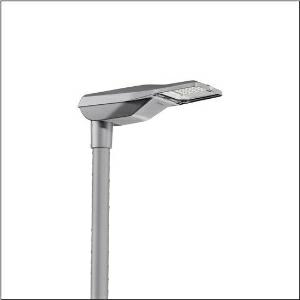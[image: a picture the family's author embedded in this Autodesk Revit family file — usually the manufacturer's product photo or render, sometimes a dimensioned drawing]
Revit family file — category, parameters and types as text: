
# Revit family: streetlight_sl_21_iq_micro___st1_0a_5xe1d21g08cb_51d7
name_source: partatom
category: Lighting Fixtures
units: mm (PartAtom-declared; Revit-internal decimal feet)

## family parameters
Cut with Voids When Loaded = No
Host = Face
Light Source = No
Part Type = Normal
Room Calculation Point = No
Round Connector Dimension = Use Diameter
Shared = No

## types (1)
- --- (1 x LED, 2380 lm, 19.4 W, 2200K)
    Apparent Load = 19 VA
    CIE Flux Codes = 37 72 97 100 100
    Color Rendering = 70
    Color Temperature = 2200K
    Default Elevation = 1800 mm
    Description = Streetlight SL 21 iQ micro, mast luminaire, primary light control with lens, of PMMA, primary optical cover: cover, of toughened safety glass, transparent, light distribution: ST1.0a, light emission: direct distribution, primary light characteristic: asymmetric, installation type: post-top, side-entry, LED, High Power LED, rated luminous flux: 2.380lm, luminous efficacy: 123lm/W, light colour: 722, colour temperature: 2200K, control gear: iQ Street-Remote, control: Street-Remote, Auto-Match, Temp-Guard, Lumen-Switch, Night-Set, Smart-Wire, Light-Fading, Desk-Remote (wireless, voltage-free reading and setting of iQ features in the workshop via application-optimized NFC function/RFID function), optimised constant luminous flux control (CLO 2.0), pre-setting: linear dimming characteristic, mains connection: 220..240V, AC, 50/60Hz, start of lifetime: 19W, end of service life: 20W, reduction: 10W, luminaire housing, of diecast aluminium, powder-coated, SITECO metallic grey (DB 702S), corrosivity category C5 high according to DIN EN ISO 12944, please order mast flange separately, inclination adjustable: 0°, 5°, 10°, 15°, sealing non-destructively replaceable, multi-level sealing system, length: 528mm, width: 235mm, height: 110mm, mast flange for spigot size: 42mm (side-entry): 5XC10008XM4, 60/48mm (side-entry/post-top): 5XC10108XM2, 76/60mm (side-entry/post-top): 5XC10108XM1, protection rating (complete): IP66, insulation class (complete): insulation class II (safety insulation), certification: CE, ENEC, ENEC+, VDE, impact resistance: IK10, permissible operating ambient temperature for outdoor applications: -40..+50°C, standard-compliant lighting for roads and squares, packaging unit: 1 piece

Light Distribution: ST1.0a
    Height = 110 mm
    Lamp = 1 x LED
    Lamp Light Flux = 2380 lm
    Lamp Power = 19.4 W
    Lamp count = 1
    Length = 528 mm
    Luminous efficacy = 123 lm/W
    Manufacturer = Siteco
    ModVariant = No
    Model = 5XE1D21G08CB
    Number of Poles = 1
    OnlyDefault = Yes
    Power Factor = 1
    Product Name = Streetlight SL 21 iQ micro | ST1.0a
    Product group = mast luminaire | pylon top
    ProductGroupID = 6100
    Protection Class = Protection class II
    Protection Degree = IP 66
    RLX_Detail_Level = 1
    RLX_Emergency_Light_Flux = 0 lm
    RLX_Emergency_Type = 0
    RLX_Emergency_Type_DB = No
    RlxData = <blob elided: 98841 chars, md5=51ffd0d3>
    Socket = socket
    Standby Power = 0 W
    System Light Flux = 2380 lm
    System Power = 19 W
    Type Comments = factory setting: luminous flux: 100 % | dim-lin: 254 | 387 mA
    Type Image = l_1006881.jpg
    URL = http://relux.com
    VarID = @adj_138819
    Voltage = 0 V
    Weight = 0.00 kg
    Width = 235 mm

## geometry (parser evidence)
native form markers: Blend x4, Sweep x10
no freeform markers — native parametric forms only
